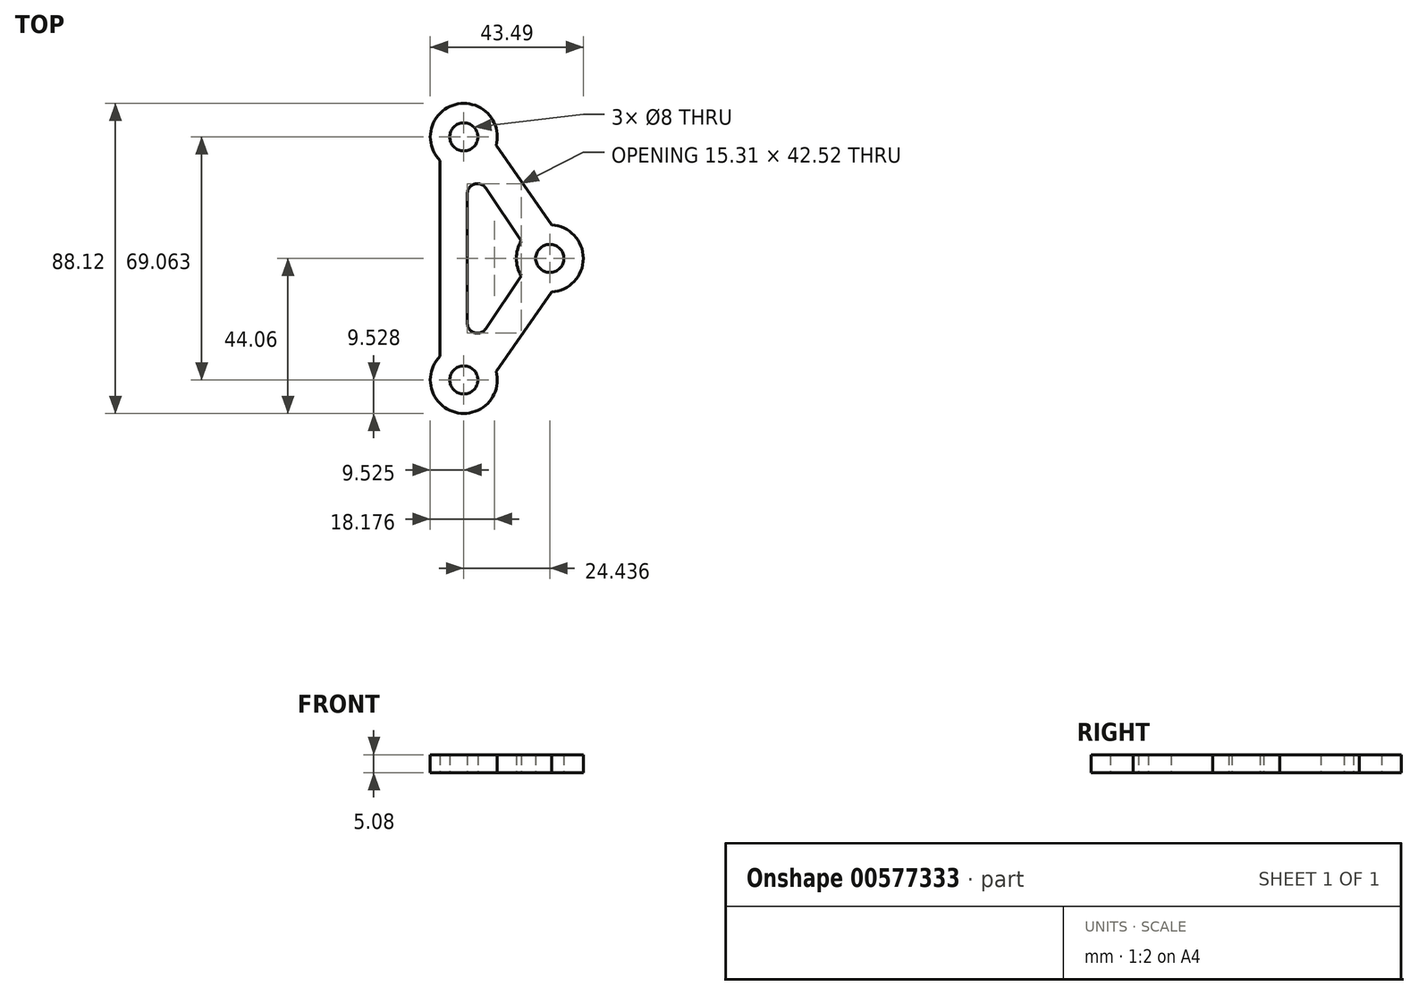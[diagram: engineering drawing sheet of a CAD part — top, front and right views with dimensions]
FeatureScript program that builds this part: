
annotation { "Feature Type Name" : "Feature", "Feature Type Description" : "" }
export const myFeature = defineFeature(function(context is Context, id is Id, definition is map)
    precondition{}
    {
        {
            var Q0;
            Q0=qCreatedBy(makeId("Top.planeOp"),FACE);
            var sketch = newSketch(context, id + "F0", { "sketchPlane" : qUnion([Q0])});
            skCircle(sketch, "E0", {"center": v(-12.19, 34.53) * mm, "radius": 4 * mm});
            skArc(sketch, "E1", {"start": v(-2.98, 32.1) * mm, "mid": v(-14.65, 43.73) * mm, "end": v(-18.94, 27.82) * mm});
            skArc(sketch, "E2", {"start": v(16.25, 0) * mm, "mid": v(12.25, 4) * mm, "end": v(8.25, 0) * mm});
            skArc(sketch, "E3", {"start": v(4.12, 4.96) * mm, "mid": v(3.08, 2.58) * mm, "end": v(2.73, 0) * mm});
            skLineSegment(sketch, "E4", {"start": v(-26.37, 0) * mm, "end": v(-11.19, 0) * mm});
            skLineSegment(sketch, "E5", {"start": v(-2.98, 32.1) * mm, "end": v(12.75, 9.51) * mm});
            skArc(sketch, "E6", {"start": v(-5.96, 20) * mm, "mid": v(-9.16, 21.14) * mm, "end": v(-11.19, 18.4) * mm});
            skLineSegment(sketch, "E7", {"start": v(-11.19, 0) * mm, "end": v(-11.19, 18.4) * mm});
            skLineSegment(sketch, "E8", {"start": v(-5.96, 20) * mm, "end": v(4.12, 4.96) * mm});
            skLineSegment(sketch, "E9", {"start": v(-18.94, 0) * mm, "end": v(-18.94, 27.82) * mm});
            skLineSegment(sketch, "E10.trimOffspring", {"start": v(2.73, 0) * mm, "end": v(8.25, 0) * mm});
            skLineSegment(sketch, "E11.trimOffspring", {"start": v(16.25, 0) * mm, "end": v(21.78, 0) * mm});
            skArc(sketch, "E12.trimOffspring", {"start": v(21.78, 0) * mm, "mid": v(19.16, 6.56) * mm, "end": v(12.75, 9.51) * mm});
            skSolve(sketch);
        }
        {
            var Q0;
            Q0 = qSketchRegion(id + "F0", true);
            extrude(context, id + "F1", {"entities" : qUnion([Q0]), "endBound" : BoundingType.SYMMETRIC, "depth" : 5.08 * mm, "offsetDistance" : 25.4 * mm});
        }
        {
            var Q0;
            Q0=makeQuery(id+"F1.opExtrude","SWEPT_BODY",BODY,{"disambiguationData":[OSD([sQuery(id+"F0.wireOp",EDGE,"E0"),sQuery(id+"F0.wireOp",EDGE,"E1"),sQuery(id+"F0.wireOp",EDGE,"E2"),sQuery(id+"F0.wireOp",EDGE,"E3"),sQuery(id+"F0.wireOp",EDGE,"E4"),sQuery(id+"F0.wireOp",EDGE,"E5"),sQuery(id+"F0.wireOp",EDGE,"E6"),sQuery(id+"F0.wireOp",EDGE,"E7"),sQuery(id+"F0.wireOp",EDGE,"E8"),sQuery(id+"F0.wireOp",EDGE,"E9"),sQuery(id+"F0.wireOp",EDGE,"E10.trimOffspring"),sQuery(id+"F0.wireOp",EDGE,"E11.trimOffspring"),sQuery(id+"F0.wireOp",EDGE,"E12.trimOffspring")])]});
            var Q1;
            Q1=qCreatedBy(makeId("Front.planeOp"),FACE);
            mirror(context, id + "F2", {"operationType" : NewBodyOperationType.ADD, "entities" : qUnion([Q0]), "mirrorPlane" : qUnion([Q1])});
        }
    });
